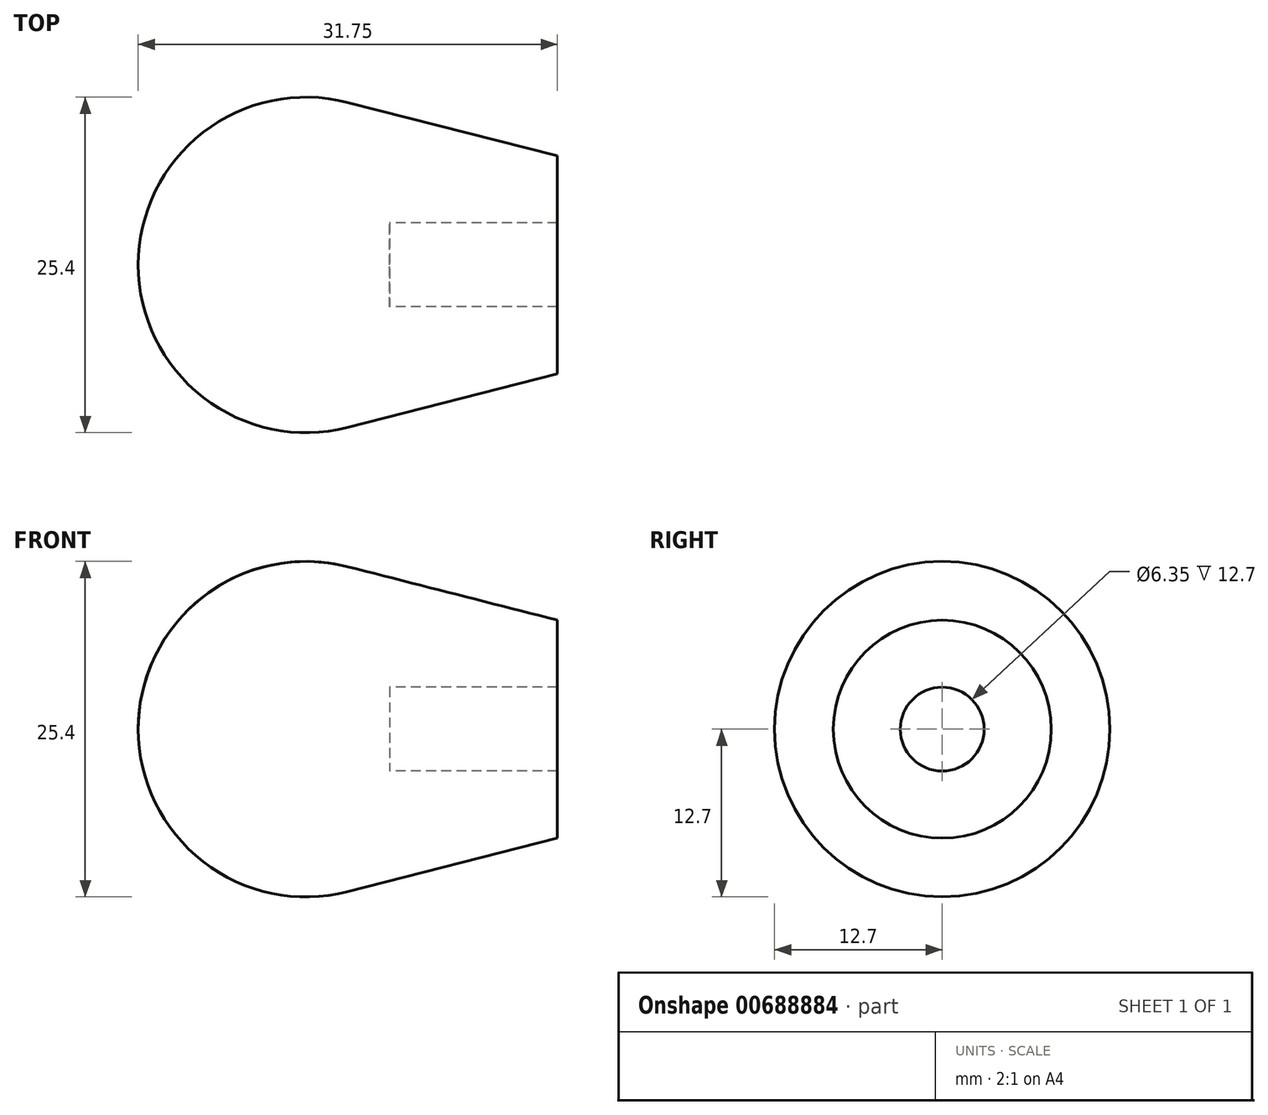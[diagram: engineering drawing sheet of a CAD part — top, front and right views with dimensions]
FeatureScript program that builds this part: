
annotation { "Feature Type Name" : "Feature", "Feature Type Description" : "" }
export const myFeature = defineFeature(function(context is Context, id is Id, definition is map)
    precondition{}
    {
        {
            var Q0;
            Q0=qCreatedBy(makeId("Front.planeOp"),FACE);
            var sketch = newSketch(context, id + "F0", { "sketchPlane" : qUnion([Q0]), "disableImprinting" : false});
            skLineSegment(sketch, "E0", {"start": v(0, 3.17) * mm, "end": v(0, 0) * mm});
            skLineSegment(sketch, "E1", {"start": v(0, 3.17) * mm, "end": v(12.7, 3.18) * mm});
            skLineSegment(sketch, "E2", {"start": v(0, 0) * mm, "end": v(-19.05, 0) * mm, "construction": true});
            skLineSegment(sketch, "E3", {"start": v(-19.05, 0) * mm, "end": v(0, 0) * mm});
            skLineSegment(sketch, "E4", {"start": v(-19.05, 0) * mm, "end": v(-19.05, -36.9) * mm, "construction": true});
            skLineSegment(sketch, "E5", {"start": v(12.7, 3.18) * mm, "end": v(12.7, 8.26) * mm});
            skLineSegment(sketch, "E6", {"start": v(12.7, 8.26) * mm, "end": v(-3.22, 12.3) * mm});
            skArc(sketch, "E7", {"start": v(-3.22, 12.3) * mm, "mid": v(-14.14, 10.03) * mm, "end": v(-19.05, 0) * mm});
            skSolve(sketch);
        }
        {
            var Q0;
            {var subQ0=sQuery(id+"F0.wireOp",EDGE,"E1");Q0=makeQuery(id+"F0.imprint","IMPRINT",FACE,{"disambiguationData":[TD([[makeQuery(id+"F0.imprint","IMPRINT",EDGE,{"derivedFrom":subQ0}),1.0]])]});}
            var Q1;
            Q1=sQuery(id+"F0.wireOp",EDGE,"E3");
            revolve(context, id + "F1", {"entities" : qUnion([Q0]), "axis" : qUnion([Q1]), "revolveType" : RevolveType.FULL});
        }
    });
